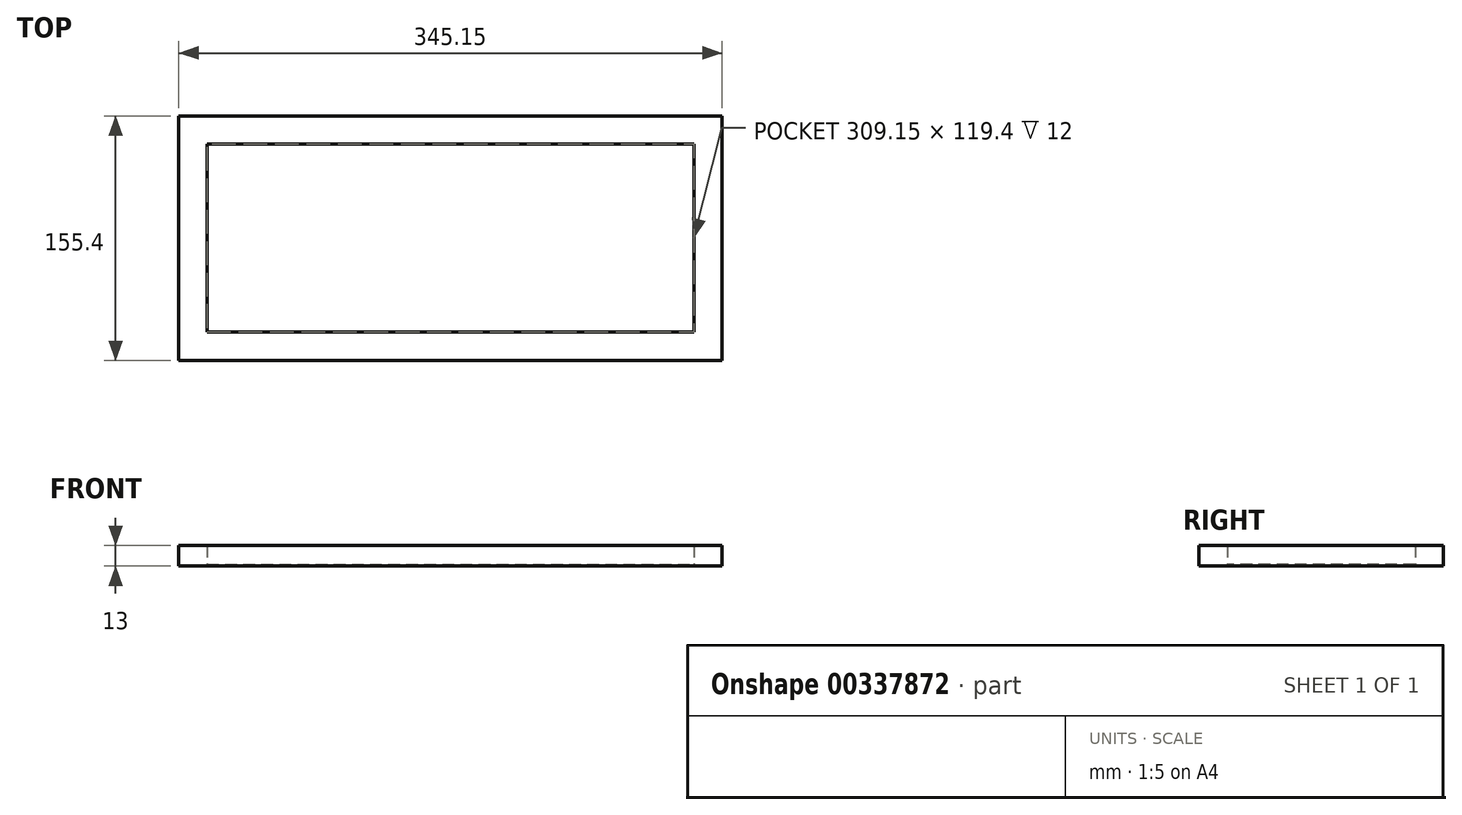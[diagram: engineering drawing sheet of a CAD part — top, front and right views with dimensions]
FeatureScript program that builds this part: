
annotation { "Feature Type Name" : "Feature", "Feature Type Description" : "" }
export const myFeature = defineFeature(function(context is Context, id is Id, definition is map)
    precondition{}
    {
        {
            var Q0;
            Q0=qCreatedBy(makeId("Top.planeOp"),FACE);
            var sketch = newSketch(context, id + "F0", { "sketchPlane" : qUnion([Q0])});
            skLineSegment(sketch, "E0.bottom", {"start": v(-148.94, 36.43) * mm, "end": v(162.2, 36.43) * mm});
            skLineSegment(sketch, "E0.top", {"start": v(-148.94, -84.97) * mm, "end": v(162.2, -84.97) * mm});
            skLineSegment(sketch, "E0.left", {"start": v(-148.94, 36.43) * mm, "end": v(-148.94, -84.97) * mm});
            skLineSegment(sketch, "E0.right", {"start": v(162.2, 36.43) * mm, "end": v(162.2, -84.97) * mm});
            skCircle(sketch, "E1", {"center": v(-116.94, -32.97) * mm, "radius": 2.5 * mm});
            skCircle(sketch, "E2", {"center": v(-61.44, -23.6) * mm, "radius": 2 * mm});
            skCircle(sketch, "E3", {"center": v(114.56, -13.79) * mm, "radius": 2.5 * mm});
            skCircle(sketch, "E4", {"center": v(74.7, -23.57) * mm, "radius": 2 * mm});
            skSolve(sketch);
        }
        {
            var Q0;
            Q0=makeQuery(id+"F0.imprint","IMPRINT",FACE,{"disambiguationData":[TD([[makeQuery(id+"F0.imprint","IMPRINT",EDGE,{"derivedFrom":sQuery(id+"F0.wireOp",EDGE,"E1")}),1.0]])]});
            var Q1;
            Q1=makeQuery(id+"F0.imprint","IMPRINT",FACE,{"disambiguationData":[TD([[makeQuery(id+"F0.imprint","IMPRINT",EDGE,{"derivedFrom":sQuery(id+"F0.wireOp",EDGE,"E2")}),1.0]])]});
            var Q2;
            Q2=makeQuery(id+"F0.imprint","IMPRINT",FACE,{"disambiguationData":[TD([[makeQuery(id+"F0.imprint","IMPRINT",EDGE,{"derivedFrom":sQuery(id+"F0.wireOp",EDGE,"E4")}),1.0]])]});
            var Q3;
            Q3=makeQuery(id+"F0.imprint","IMPRINT",FACE,{"disambiguationData":[TD([[makeQuery(id+"F0.imprint","IMPRINT",EDGE,{"derivedFrom":sQuery(id+"F0.wireOp",EDGE,"E3")}),1.0]])]});
            var Q4;
            Q4=makeQuery(id+"F0.imprint","IMPRINT",FACE,{"disambiguationData":[TD([[makeQuery(id+"F0.imprint","IMPRINT",EDGE,{"derivedFrom":sQuery(id+"F0.wireOp",EDGE,"E0.bottom")}),-1.0]])]});
            extrude(context, id + "F1", {"entities" : qUnion([Q0, Q1, Q2, Q3, Q4]), "depth" : 13 * mm});
        }
        {
            var Q0;
            Q0=makeQuery(id+"F1.opExtrude","CAP_FACE",FACE,{"disambiguationData":[OSD([sQuery(id+"F0.wireOp",EDGE,"E0.bottom"),sQuery(id+"F0.wireOp",EDGE,"E0.top"),sQuery(id+"F0.wireOp",EDGE,"E0.left"),sQuery(id+"F0.wireOp",EDGE,"E0.right"),sQuery(id+"F0.wireOp",EDGE,"E1"),sQuery(id+"F0.wireOp",EDGE,"E2"),sQuery(id+"F0.wireOp",EDGE,"E3"),sQuery(id+"F0.wireOp",EDGE,"E4")])],"isStart":false});
            shell(context, id + "F2", {"entities" : qUnion([Q0]), "thickness" : 1 * mm});
        }
        {
            var Q0;
            Q0=sQuery(id+"F0.wireOp",EDGE,"E1");
            var Q1;
            Q1=sQuery(id+"F0.wireOp",EDGE,"E2");
            var Q2;
            Q2=sQuery(id+"F0.wireOp",EDGE,"E3");
            var Q3;
            Q3=sQuery(id+"F0.wireOp",EDGE,"E4");
            extrude(context, id + "F3", {"bodyType" : ToolBodyType.SURFACE, "surfaceEntities" : qUnion([Q0, Q1, Q2, Q3]), "depth" : 15.24 * mm});
        }
        {
            var Q0;
            Q0=makeQuery(id+"F1.opExtrude","SWEPT_FACE",FACE,{"disambiguationData":[OSD([sQuery(id+"F0.wireOp",EDGE,"E0.top")])]});
            extrude(context, id + "F4", {"entities" : qUnion([Q0]), "operationType" : NewBodyOperationType.ADD, "depth" : 17 * mm});
        }
        {
            var Q0;
            {var subQ0=sQuery(id+"F0.wireOp",EDGE,"E0.left");Q0=makeQuery(id+"F4.boolean.opBoolean","MERGE",FACE,{"derivedFrom":[makeQuery(id+"F1.opExtrude","SWEPT_FACE",FACE,{"disambiguationData":[OSD([subQ0])]}),makeQuery(id+"F4.opExtrude","SWEPT_FACE",FACE,{"disambiguationData":[OSD([sQuery(id+"F0.wireOp",EDGE,"E0.top"),subQ0])]})]});}
            extrude(context, id + "F5", {"entities" : qUnion([Q0]), "operationType" : NewBodyOperationType.ADD, "depth" : 17 * mm});
        }
        {
            var Q0;
            {var subQ0=sQuery(id+"F0.wireOp",EDGE,"E0.right");Q0=makeQuery(id+"F4.boolean.opBoolean","MERGE",FACE,{"derivedFrom":[makeQuery(id+"F1.opExtrude","SWEPT_FACE",FACE,{"disambiguationData":[OSD([subQ0])]}),makeQuery(id+"F4.opExtrude","SWEPT_FACE",FACE,{"disambiguationData":[OSD([sQuery(id+"F0.wireOp",EDGE,"E0.top"),subQ0])]})]});}
            extrude(context, id + "F6", {"entities" : qUnion([Q0]), "operationType" : NewBodyOperationType.ADD, "depth" : 17 * mm});
        }
        {
            var Q0;
            {var subQ0=sQuery(id+"F0.wireOp",EDGE,"E0.bottom");Q0=makeQuery(id+"F6.boolean.opBoolean","MERGE",FACE,{"derivedFrom":[makeQuery(id+"F5.boolean.opBoolean","MERGE",FACE,{"derivedFrom":[makeQuery(id+"F1.opExtrude","SWEPT_FACE",FACE,{"disambiguationData":[OSD([subQ0])]}),makeQuery(id+"F5.opExtrude","SWEPT_FACE",FACE,{"disambiguationData":[OSD([subQ0,sQuery(id+"F0.wireOp",EDGE,"E0.left")])]})]}),makeQuery(id+"F6.opExtrude","SWEPT_FACE",FACE,{"disambiguationData":[OSD([subQ0,sQuery(id+"F0.wireOp",EDGE,"E0.right")])]})]});}
            extrude(context, id + "F7", {"entities" : qUnion([Q0]), "operationType" : NewBodyOperationType.ADD, "depth" : 17 * mm});
        }
    });
